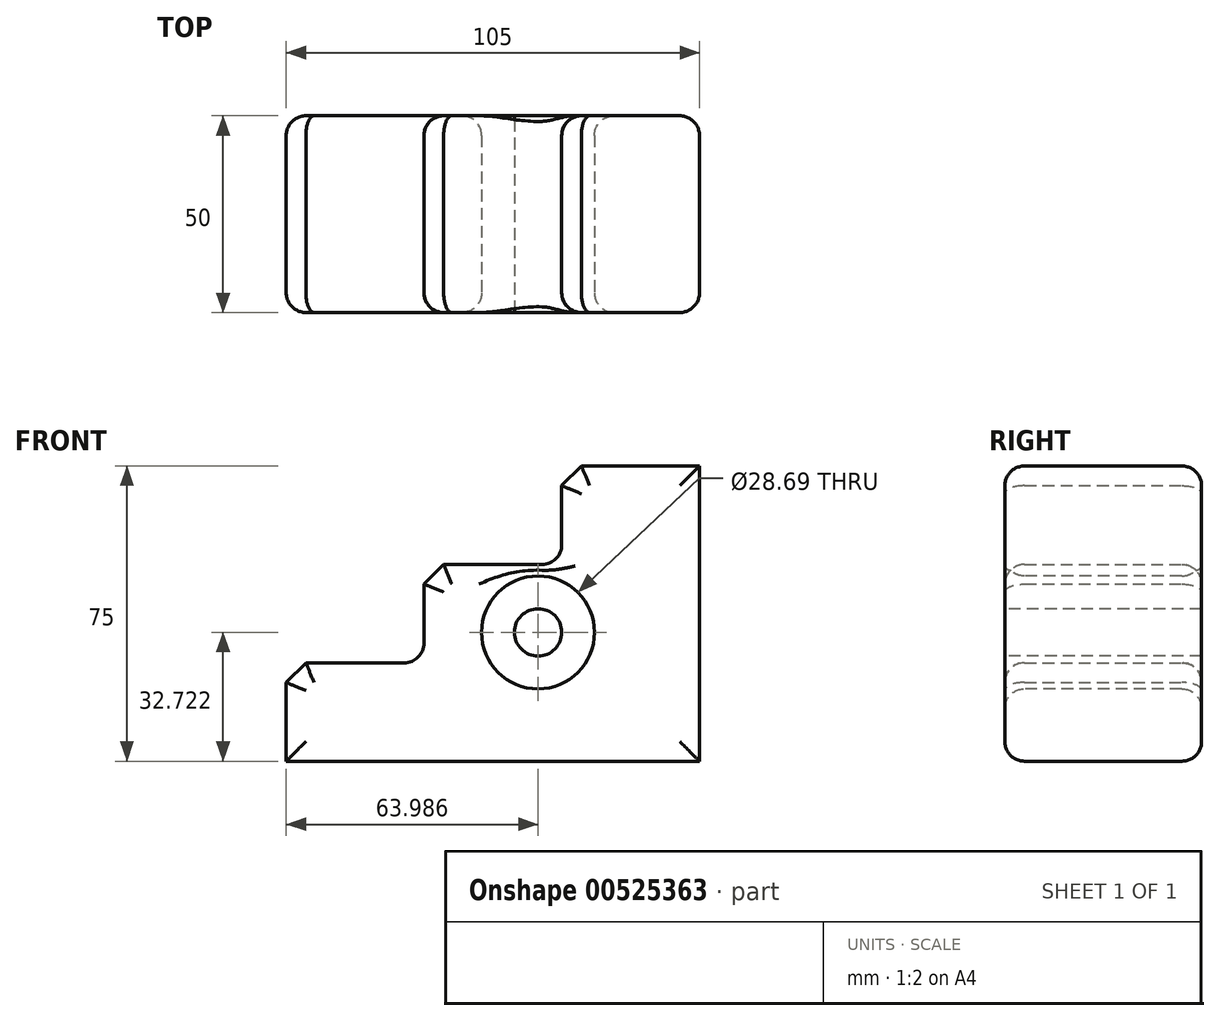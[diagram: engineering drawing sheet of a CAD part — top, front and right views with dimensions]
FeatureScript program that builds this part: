
annotation { "Feature Type Name" : "Feature", "Feature Type Description" : "" }
export const myFeature = defineFeature(function(context is Context, id is Id, definition is map)
    precondition{}
    {
        {
            var Q0;
            Q0=qCreatedBy(makeId("Front.planeOp"),FACE);
            var sketch = newSketch(context, id + "F0", { "sketchPlane" : qUnion([Q0])});
            skLineSegment(sketch, "E0", {"start": v(-45.12, 0) * mm, "end": v(59.88, 0) * mm});
            skLineSegment(sketch, "E1", {"start": v(59.88, 0) * mm, "end": v(59.88, 75) * mm});
            skLineSegment(sketch, "E2", {"start": v(59.88, 75) * mm, "end": v(24.88, 75) * mm});
            skLineSegment(sketch, "E3", {"start": v(24.88, 75) * mm, "end": v(24.88, 55) * mm});
            skLineSegment(sketch, "E4", {"start": v(-10.12, 50) * mm, "end": v(19.88, 50) * mm});
            skLineSegment(sketch, "E5", {"start": v(-10.12, 50) * mm, "end": v(-10.12, 30) * mm});
            skLineSegment(sketch, "E6", {"start": v(-15.12, 25) * mm, "end": v(-45.12, 25) * mm});
            skLineSegment(sketch, "E7", {"start": v(-45.12, 25) * mm, "end": v(-45.12, 0) * mm});
            skPoint(sketch, "E8.orphan", {"position": v(-54.67, 0) * mm});
            skPoint(sketch, "E9.visualSharp", {"position": v(-10.12, 25) * mm});
            skArc(sketch, "E9.filletArc", {"start": v(-15.12, 25) * mm, "mid": v(-11.59, 26.46) * mm, "end": v(-10.12, 30) * mm});
            skPoint(sketch, "E10.visualSharp", {"position": v(24.88, 50) * mm});
            skArc(sketch, "E10.filletArc", {"start": v(19.88, 50) * mm, "mid": v(23.41, 51.46) * mm, "end": v(24.88, 55) * mm});
            skSolve(sketch);
        }
        {
            var Q0;
            Q0 = qSketchRegion(id + "F0", true);
            extrude(context, id + "F1", {"entities" : qUnion([Q0]), "endBound" : BoundingType.SYMMETRIC, "depth" : 50 * mm, "offsetDistance" : 25.4 * mm});
        }
        {
            var Q0;
            Q0=makeQuery(id+"F1.opExtrude","CAP_FACE",FACE,{"disambiguationData":[OSD([sQuery(id+"F0.wireOp",EDGE,"E0"),sQuery(id+"F0.wireOp",EDGE,"E1"),sQuery(id+"F0.wireOp",EDGE,"E2"),sQuery(id+"F0.wireOp",EDGE,"E3"),sQuery(id+"F0.wireOp",EDGE,"E4"),sQuery(id+"F0.wireOp",EDGE,"E5"),sQuery(id+"F0.wireOp",EDGE,"E6"),sQuery(id+"F0.wireOp",EDGE,"E7"),sQuery(id+"F0.wireOp",EDGE,"E9.filletArc"),sQuery(id+"F0.wireOp",EDGE,"E10.filletArc")])],"isStart":false});
            var sketch = newSketch(context, id + "F2", { "sketchPlane" : qUnion([Q0])});
            skCircle(sketch, "E11", {"center": v(18.87, 32.72) * mm, "radius": 6 * mm});
            skCircle(sketch, "E12", {"center": v(18.87, 32.72) * mm, "radius": 14.34 * mm});
            skSolve(sketch);
        }
        {
            var Q0;
            Q0 = qSketchRegion(id + "F2", true);
            extrude(context, id + "F3", {"entities" : qUnion([Q0]), "operationType" : NewBodyOperationType.REMOVE, "endBound" : BoundingType.UP_TO_NEXT, "oppositeDirection" : true, "depth" : 25 * mm, "offsetDistance" : 25 * mm});
        }
        {
            var Q0;
            Q0=makeQuery(id+"F1.opExtrude","SWEPT_EDGE",EDGE,{"disambiguationData":[OSD([sQuery(id+"F0.wireOp",EDGE,"E6"),sQuery(id+"F0.wireOp",EDGE,"E7")])]});
            var Q1;
            Q1=makeQuery(id+"F1.opExtrude","SWEPT_EDGE",EDGE,{"disambiguationData":[OSD([sQuery(id+"F0.wireOp",EDGE,"E4"),sQuery(id+"F0.wireOp",EDGE,"E5")])]});
            var Q2;
            Q2=makeQuery(id+"F1.opExtrude","SWEPT_EDGE",EDGE,{"disambiguationData":[OSD([sQuery(id+"F0.wireOp",EDGE,"E2"),sQuery(id+"F0.wireOp",EDGE,"E3")])]});
            chamfer(context, id + "F4", {"entities" : qUnion([Q0, Q1, Q2]), "width" : 5 * mm, "tangentPropagation" : true});
        }
        {
            var Q0;
            Q0=makeQuery(id+"F1.opExtrude","CAP_EDGE",EDGE,{"disambiguationData":[OSD([sQuery(id+"F0.wireOp",EDGE,"E2")])],"isStart":false});
            var Q1;
            {var subQ0=sQuery(id+"F0.wireOp",EDGE,"E9.filletArc");var subQ1=sQuery(id+"F0.wireOp",EDGE,"E7");var subQ2=sQuery(id+"F0.wireOp",EDGE,"E6");var subQ3=sQuery(id+"F0.wireOp",EDGE,"E5");var subQ4=sQuery(id+"F0.wireOp",EDGE,"E4");var subQ5=sQuery(id+"F0.wireOp",EDGE,"E10.filletArc");var subQ6=sQuery(id+"F0.wireOp",EDGE,"E0");var subQ7=sQuery(id+"F0.wireOp",EDGE,"E3");var subQ8=sQuery(id+"F0.wireOp",EDGE,"E1");var subQ9=sQuery(id+"F0.wireOp",EDGE,"E2");Q1=makeQuery(id+"F4.opChamfer","BLEND_EDGE",EDGE,{"blendedFrom":[makeQuery(id+"F1.opExtrude","SWEPT_EDGE",EDGE,{"disambiguationData":[OSD([subQ9,subQ7])]}),makeQuery(id+"F3.boolean.opBoolean","SPLIT",FACE,{"disambiguationData":[TD([makeQuery(id+"F1.opExtrude","SWEPT_FACE",FACE,{"disambiguationData":[OSD([subQ6])]})])],"derivedFrom":makeQuery(id+"F1.opExtrude","CAP_FACE",FACE,{"disambiguationData":[OSD([subQ6,subQ8,subQ9,subQ7,subQ4,subQ3,subQ2,subQ1,subQ0,subQ5])],"isStart":false})})],"blendedInto":[makeQuery(id+"F3.boolean.opBoolean","SPLIT",FACE,{"disambiguationData":[TD([makeQuery(id+"F1.opExtrude","SWEPT_FACE",FACE,{"disambiguationData":[OSD([subQ6])]})])],"derivedFrom":makeQuery(id+"F1.opExtrude","CAP_FACE",FACE,{"disambiguationData":[OSD([subQ6,subQ8,subQ9,subQ7,subQ4,subQ3,subQ2,subQ1,subQ0,subQ5])],"isStart":false})})]});}
            var Q2;
            Q2=makeQuery(id+"F1.opExtrude","CAP_EDGE",EDGE,{"disambiguationData":[OSD([sQuery(id+"F0.wireOp",EDGE,"E3")])],"isStart":false});
            var Q3;
            Q3=makeQuery(id+"F1.opExtrude","CAP_EDGE",EDGE,{"disambiguationData":[OSD([sQuery(id+"F0.wireOp",EDGE,"E10.filletArc")])],"isStart":false});
            var Q4;
            {var subQ0=sQuery(id+"F0.wireOp",EDGE,"E9.filletArc");var subQ1=sQuery(id+"F0.wireOp",EDGE,"E7");var subQ2=sQuery(id+"F0.wireOp",EDGE,"E6");var subQ3=sQuery(id+"F0.wireOp",EDGE,"E5");var subQ4=sQuery(id+"F0.wireOp",EDGE,"E4");var subQ5=sQuery(id+"F0.wireOp",EDGE,"E10.filletArc");var subQ6=sQuery(id+"F0.wireOp",EDGE,"E0");var subQ7=sQuery(id+"F0.wireOp",EDGE,"E3");var subQ8=sQuery(id+"F0.wireOp",EDGE,"E1");var subQ9=sQuery(id+"F0.wireOp",EDGE,"E2");Q4=makeQuery(id+"F4.opChamfer","BLEND_EDGE",EDGE,{"blendedFrom":[makeQuery(id+"F1.opExtrude","SWEPT_EDGE",EDGE,{"disambiguationData":[OSD([subQ4,subQ3])]}),makeQuery(id+"F3.boolean.opBoolean","SPLIT",FACE,{"disambiguationData":[TD([makeQuery(id+"F1.opExtrude","SWEPT_FACE",FACE,{"disambiguationData":[OSD([subQ6])]})])],"derivedFrom":makeQuery(id+"F1.opExtrude","CAP_FACE",FACE,{"disambiguationData":[OSD([subQ6,subQ8,subQ9,subQ7,subQ4,subQ3,subQ2,subQ1,subQ0,subQ5])],"isStart":false})})],"blendedInto":[makeQuery(id+"F3.boolean.opBoolean","SPLIT",FACE,{"disambiguationData":[TD([makeQuery(id+"F1.opExtrude","SWEPT_FACE",FACE,{"disambiguationData":[OSD([subQ6])]})])],"derivedFrom":makeQuery(id+"F1.opExtrude","CAP_FACE",FACE,{"disambiguationData":[OSD([subQ6,subQ8,subQ9,subQ7,subQ4,subQ3,subQ2,subQ1,subQ0,subQ5])],"isStart":false})})]});}
            var Q5;
            Q5=makeQuery(id+"F1.opExtrude","CAP_EDGE",EDGE,{"disambiguationData":[OSD([sQuery(id+"F0.wireOp",EDGE,"E5")])],"isStart":false});
            var Q6;
            {var subQ0=sQuery(id+"F0.wireOp",EDGE,"E9.filletArc");var subQ1=sQuery(id+"F0.wireOp",EDGE,"E7");var subQ2=sQuery(id+"F0.wireOp",EDGE,"E6");var subQ3=sQuery(id+"F0.wireOp",EDGE,"E5");var subQ4=sQuery(id+"F0.wireOp",EDGE,"E4");var subQ5=sQuery(id+"F0.wireOp",EDGE,"E10.filletArc");var subQ6=sQuery(id+"F0.wireOp",EDGE,"E0");var subQ7=sQuery(id+"F0.wireOp",EDGE,"E3");var subQ8=sQuery(id+"F0.wireOp",EDGE,"E1");var subQ9=sQuery(id+"F0.wireOp",EDGE,"E2");Q6=makeQuery(id+"F3.boolean.opBoolean","SPLIT",FACE,{"disambiguationData":[TD([makeQuery(id+"F1.opExtrude","SWEPT_FACE",FACE,{"disambiguationData":[OSD([subQ6])]})])],"derivedFrom":makeQuery(id+"F1.opExtrude","CAP_FACE",FACE,{"disambiguationData":[OSD([subQ6,subQ8,subQ9,subQ7,subQ4,subQ3,subQ2,subQ1,subQ0,subQ5])],"isStart":false})});}
            var Q7;
            {var subQ0=sQuery(id+"F0.wireOp",EDGE,"E9.filletArc");var subQ1=sQuery(id+"F0.wireOp",EDGE,"E7");var subQ2=sQuery(id+"F0.wireOp",EDGE,"E6");var subQ3=sQuery(id+"F0.wireOp",EDGE,"E5");var subQ4=sQuery(id+"F0.wireOp",EDGE,"E4");var subQ5=sQuery(id+"F0.wireOp",EDGE,"E10.filletArc");var subQ6=sQuery(id+"F0.wireOp",EDGE,"E0");var subQ7=sQuery(id+"F0.wireOp",EDGE,"E3");var subQ8=sQuery(id+"F0.wireOp",EDGE,"E1");var subQ9=sQuery(id+"F0.wireOp",EDGE,"E2");Q7=makeQuery(id+"F3.boolean.opBoolean","SPLIT",FACE,{"disambiguationData":[TD([makeQuery(id+"F1.opExtrude","SWEPT_FACE",FACE,{"disambiguationData":[OSD([subQ6])]})])],"derivedFrom":makeQuery(id+"F1.opExtrude","CAP_FACE",FACE,{"disambiguationData":[OSD([subQ6,subQ8,subQ9,subQ7,subQ4,subQ3,subQ2,subQ1,subQ0,subQ5])],"isStart":true})});}
            fillet(context, id + "F5", {"entities" : qUnion([Q0, Q1, Q2, Q3, Q4, Q5, Q6, Q7]), "radius" : 5 * mm, "tangentPropagation" : true, "allowEdgeOverflow" : false});
        }
    });
